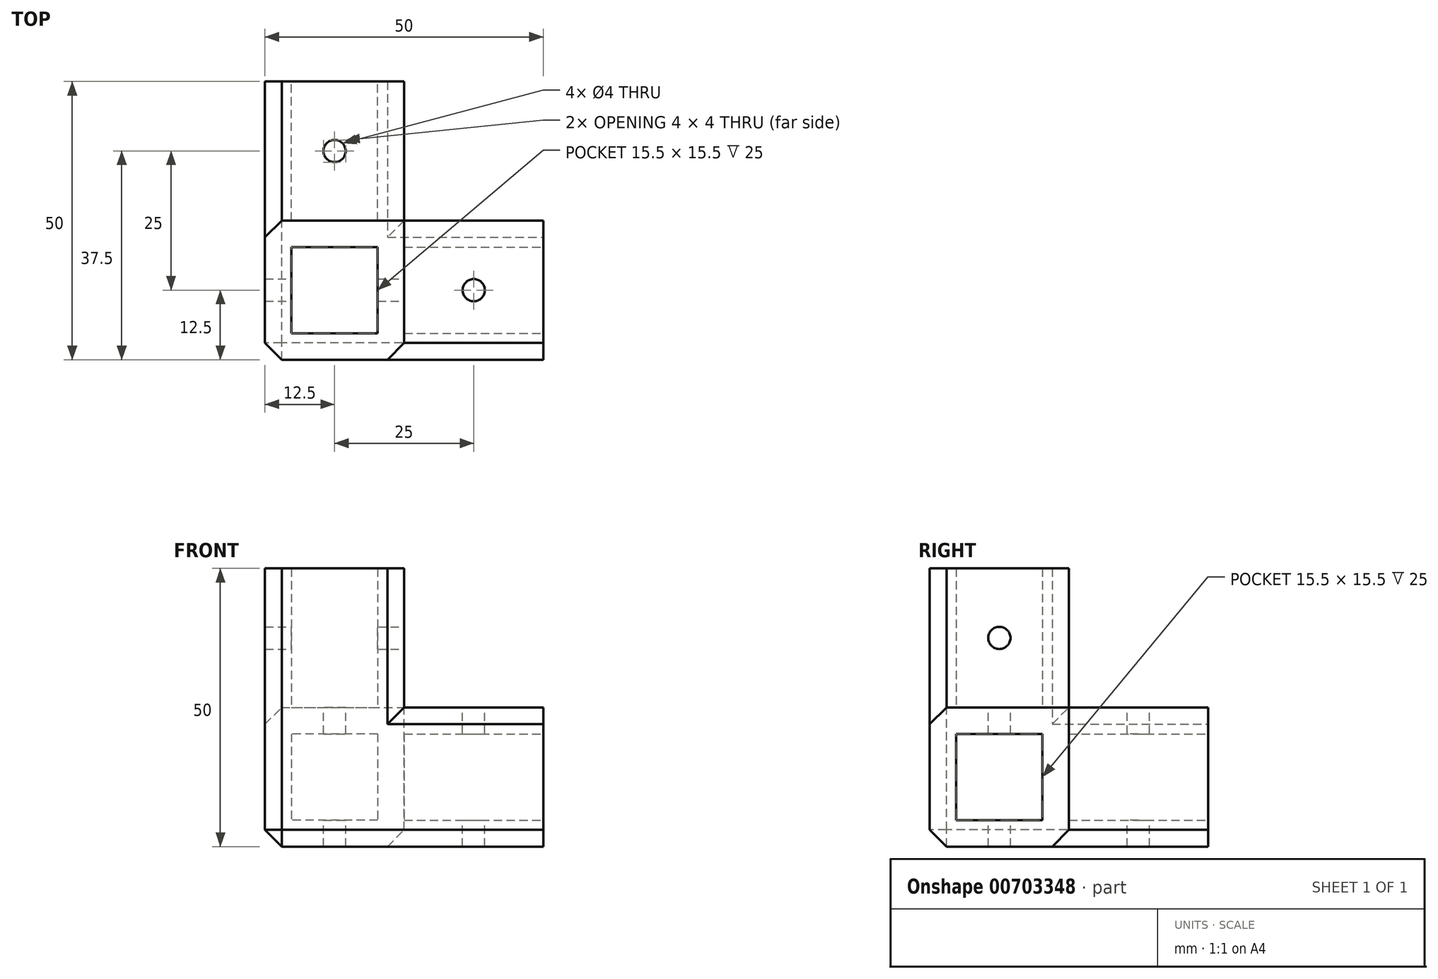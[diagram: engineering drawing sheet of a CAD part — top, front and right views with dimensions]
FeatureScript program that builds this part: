
annotation { "Feature Type Name" : "Feature", "Feature Type Description" : "" }
export const myFeature = defineFeature(function(context is Context, id is Id, definition is map)
    precondition{}
    {
        {
            var Q0;
            Q0=qCreatedBy(makeId("Top.planeOp"),FACE);
            var sketch = newSketch(context, id + "F0", { "sketchPlane" : qUnion([Q0])});
            skLineSegment(sketch, "E0", {"start": v(-60, 0) * mm, "end": v(-60, 50) * mm});
            skLineSegment(sketch, "E1", {"start": v(-60, 50) * mm, "end": v(-35, 50) * mm});
            skLineSegment(sketch, "E2", {"start": v(-35, 50) * mm, "end": v(-35, 25) * mm});
            skLineSegment(sketch, "E3", {"start": v(-35, 25) * mm, "end": v(-10, 25) * mm});
            skLineSegment(sketch, "E4", {"start": v(-10, 25) * mm, "end": v(-10, 0) * mm});
            skLineSegment(sketch, "E5", {"start": v(-10, 0) * mm, "end": v(-60, 0) * mm});
            skLineSegment(sketch, "E6", {"start": v(-60, 25) * mm, "end": v(-35, 25) * mm});
            skLineSegment(sketch, "E7", {"start": v(-35, 25) * mm, "end": v(-35, 0) * mm});
            skLineSegment(sketch, "E8", {"start": v(-60, 0) * mm, "end": v(-35, 25) * mm, "construction": true});
            skLineSegment(sketch, "E9", {"start": v(-60, 25) * mm, "end": v(-35, 0) * mm, "construction": true});
            skLineSegment(sketch, "E10.bottom", {"start": v(-55.25, 20.25) * mm, "end": v(-39.75, 20.25) * mm});
            skLineSegment(sketch, "E10.top", {"start": v(-55.25, 4.75) * mm, "end": v(-39.75, 4.75) * mm});
            skLineSegment(sketch, "E10.left", {"start": v(-55.25, 20.25) * mm, "end": v(-55.25, 4.75) * mm});
            skLineSegment(sketch, "E10.right", {"start": v(-39.75, 20.25) * mm, "end": v(-39.75, 4.75) * mm});
            skPoint(sketch, "E10.middle", {"position": v(-47.5, 12.5) * mm});
            skLineSegment(sketch, "E11", {"start": v(-35, 0) * mm, "end": v(-10, 25) * mm, "construction": true});
            skLineSegment(sketch, "E12", {"start": v(-10, 0) * mm, "end": v(-60, 50) * mm, "construction": true});
            skLineSegment(sketch, "E13", {"start": v(-60, 25) * mm, "end": v(-35, 50) * mm, "construction": true});
            skCircle(sketch, "E14", {"center": v(-47.5, 37.5) * mm, "radius": 2 * mm});
            skCircle(sketch, "E15", {"center": v(-22.5, 12.5) * mm, "radius": 2 * mm});
            skSolve(sketch);
        }
        {
            var Q0;
            {var subQ0=sQuery(id+"F0.wireOp",EDGE,"E1");Q0=makeQuery(id+"F0.imprint","IMPRINT",FACE,{"disambiguationData":[TD([[makeQuery(id+"F0.imprint","IMPRINT",EDGE,{"derivedFrom":subQ0}),-1.0]])]});}
            var Q1;
            Q1=makeQuery(id+"F0.imprint","IMPRINT",FACE,{"disambiguationData":[TD([[makeQuery(id+"F0.imprint","IMPRINT",EDGE,{"derivedFrom":sQuery(id+"F0.wireOp",EDGE,"E3")}),-1.0]])]});
            var Q2;
            {var subQ1=sQuery(id+"F0.wireOp",EDGE,"E6");Q2=makeQuery(id+"F0.imprint","IMPRINT",FACE,{"disambiguationData":[TD([[makeQuery(id+"F0.imprint","IMPRINT",EDGE,{"derivedFrom":subQ1}),-1.0]])]});}
            var Q3;
            Q3=makeQuery(id+"F0.imprint","IMPRINT",FACE,{"disambiguationData":[TD([[makeQuery(id+"F0.imprint","IMPRINT",EDGE,{"derivedFrom":sQuery(id+"F0.wireOp",EDGE,"E10.bottom")}),-1.0]])]});
            extrude(context, id + "F1", {"entities" : qUnion([Q0, Q1, Q2, Q3]), "oppositeDirection" : true, "depth" : 25 * mm, "offsetDistance" : 25 * mm});
        }
        {
            var Q0;
            Q0=makeQuery(id+"F1.opExtrude","SWEPT_FACE",FACE,{"disambiguationData":[OSD([sQuery(id+"F0.wireOp",EDGE,"E4")])]});
            var sketch = newSketch(context, id + "F2", { "sketchPlane" : qUnion([Q0])});
            skLineSegment(sketch, "E16", {"start": v(0, 0) * mm, "end": v(25, -25) * mm, "construction": true});
            skLineSegment(sketch, "E17", {"start": v(25, -25) * mm, "end": v(25, 0) * mm, "construction": true});
            skLineSegment(sketch, "E18", {"start": v(25, 0) * mm, "end": v(0, -25) * mm, "construction": true});
            skLineSegment(sketch, "E19.bottom", {"start": v(4.75, -4.75) * mm, "end": v(20.25, -4.75) * mm});
            skLineSegment(sketch, "E19.top", {"start": v(4.75, -20.25) * mm, "end": v(20.25, -20.25) * mm});
            skLineSegment(sketch, "E19.left", {"start": v(4.75, -4.75) * mm, "end": v(4.75, -20.25) * mm});
            skLineSegment(sketch, "E19.right", {"start": v(20.25, -4.75) * mm, "end": v(20.25, -20.25) * mm});
            skPoint(sketch, "E19.middle", {"position": v(12.5, -12.5) * mm});
            skSolve(sketch);
        }
        {
            var Q0;
            Q0=makeQuery(id+"F2.imprint","IMPRINT",FACE,{"disambiguationData":[TD([[makeQuery(id+"F2.imprint","IMPRINT",EDGE,{"derivedFrom":sQuery(id+"F2.wireOp",EDGE,"E19.bottom")}),-1.0]])]});
            extrude(context, id + "F3", {"entities" : qUnion([Q0]), "operationType" : NewBodyOperationType.REMOVE, "oppositeDirection" : true, "depth" : 25 * mm, "offsetDistance" : 25 * mm});
        }
        {
            var Q0;
            Q0=makeQuery(id+"F1.opExtrude","SWEPT_FACE",FACE,{"disambiguationData":[OSD([sQuery(id+"F0.wireOp",EDGE,"E1")])]});
            var sketch = newSketch(context, id + "F4", { "sketchPlane" : qUnion([Q0])});
            skLineSegment(sketch, "E20", {"start": v(35, 0) * mm, "end": v(60, -25) * mm, "construction": true});
            skLineSegment(sketch, "E21", {"start": v(60, -25) * mm, "end": v(60, 0) * mm, "construction": true});
            skLineSegment(sketch, "E22", {"start": v(60, 0) * mm, "end": v(35, -25) * mm, "construction": true});
            skLineSegment(sketch, "E23.bottom", {"start": v(39.75, -4.75) * mm, "end": v(55.25, -4.75) * mm});
            skLineSegment(sketch, "E23.top", {"start": v(39.75, -20.25) * mm, "end": v(55.25, -20.25) * mm});
            skLineSegment(sketch, "E23.left", {"start": v(39.75, -4.75) * mm, "end": v(39.75, -20.25) * mm});
            skLineSegment(sketch, "E23.right", {"start": v(55.25, -4.75) * mm, "end": v(55.25, -20.25) * mm});
            skPoint(sketch, "E23.middle", {"position": v(47.5, -12.5) * mm});
            skSolve(sketch);
        }
        {
            var Q0;
            Q0=makeQuery(id+"F4.imprint","IMPRINT",FACE,{"disambiguationData":[TD([[makeQuery(id+"F4.imprint","IMPRINT",EDGE,{"derivedFrom":sQuery(id+"F4.wireOp",EDGE,"E23.bottom")}),-1.0]])]});
            extrude(context, id + "F5", {"entities" : qUnion([Q0]), "operationType" : NewBodyOperationType.REMOVE, "oppositeDirection" : true, "depth" : 25 * mm, "offsetDistance" : 25 * mm});
        }
        {
            var Q0;
            {var subQ1=sQuery(id+"F0.wireOp",EDGE,"E6");Q0=makeQuery(id+"F0.imprint","IMPRINT",FACE,{"disambiguationData":[TD([[makeQuery(id+"F0.imprint","IMPRINT",EDGE,{"derivedFrom":subQ1}),-1.0]])]});}
            extrude(context, id + "F6", {"entities" : qUnion([Q0]), "operationType" : NewBodyOperationType.ADD, "depth" : 25 * mm, "offsetDistance" : 25 * mm});
        }
        {
            var Q0;
            Q0=makeQuery(id+"F6.opExtrude","SWEPT_FACE",FACE,{"disambiguationData":[OSD([sQuery(id+"F0.wireOp",EDGE,"E7")])]});
            var sketch = newSketch(context, id + "F7", { "sketchPlane" : qUnion([Q0])});
            skLineSegment(sketch, "E24", {"start": v(25, 0) * mm, "end": v(0, 25) * mm, "construction": true});
            skLineSegment(sketch, "E25", {"start": v(0, 25) * mm, "end": v(25, 25) * mm, "construction": true});
            skLineSegment(sketch, "E26", {"start": v(25, 25) * mm, "end": v(0, 0) * mm, "construction": true});
            skCircle(sketch, "E27", {"center": v(12.5, 12.5) * mm, "radius": 2 * mm});
            skSolve(sketch);
        }
        {
            var Q0;
            {var subQ0=sQuery(id+"F0.wireOp",EDGE,"E5");var subQ1=sQuery(id+"F0.wireOp",EDGE,"E0");Q0=makeQuery(id+"F6.boolean.opBoolean","MERGE",EDGE,{"derivedFrom":[makeQuery(id+"F1.opExtrude","SWEPT_EDGE",EDGE,{"disambiguationData":[OSD([subQ1,subQ0])]}),makeQuery(id+"F6.opExtrude","SWEPT_EDGE",EDGE,{"disambiguationData":[OSD([subQ1,subQ0])]})]});}
            var Q1;
            Q1=makeQuery(id+"F1.opExtrude","CAP_EDGE",EDGE,{"disambiguationData":[OSD([sQuery(id+"F0.wireOp",EDGE,"E5")])],"isStart":false});
            var Q2;
            Q2=makeQuery(id+"F1.opExtrude","CAP_EDGE",EDGE,{"disambiguationData":[OSD([sQuery(id+"F0.wireOp",EDGE,"E0")])],"isStart":false});
            var Q3;
            Q3=makeQuery(id+"F6.opExtrude","SWEPT_EDGE",EDGE,{"disambiguationData":[OSD([sQuery(id+"F0.wireOp",EDGE,"E5"),sQuery(id+"F0.wireOp",EDGE,"E7")])]});
            var Q4;
            Q4=makeQuery(id+"F1.opExtrude","CAP_EDGE",EDGE,{"disambiguationData":[OSD([sQuery(id+"F0.wireOp",EDGE,"E5")])],"isStart":true});
            var Q5;
            Q5=makeQuery(id+"F1.opExtrude","CAP_EDGE",EDGE,{"disambiguationData":[OSD([sQuery(id+"F0.wireOp",EDGE,"E2")])],"isStart":false});
            var Q6;
            Q6=makeQuery(id+"F1.opExtrude","CAP_EDGE",EDGE,{"disambiguationData":[OSD([sQuery(id+"F0.wireOp",EDGE,"E3")])],"isStart":false});
            var Q7;
            Q7=makeQuery(id+"F1.opExtrude","CAP_EDGE",EDGE,{"disambiguationData":[OSD([sQuery(id+"F0.wireOp",EDGE,"E0")])],"isStart":true});
            var Q8;
            Q8=makeQuery(id+"F6.opExtrude","SWEPT_EDGE",EDGE,{"disambiguationData":[OSD([sQuery(id+"F0.wireOp",EDGE,"E0"),sQuery(id+"F0.wireOp",EDGE,"E6")])]});
            chamfer(context, id + "F8", {"entities" : qUnion([Q0, Q1, Q2, Q3, Q4, Q5, Q6, Q7, Q8]), "width" : 3 * mm, "tangentPropagation" : true});
        }
        {
            var Q0;
            Q0=makeQuery(id+"F7.imprint","IMPRINT",FACE,{"disambiguationData":[TD([[makeQuery(id+"F7.imprint","IMPRINT",EDGE,{"derivedFrom":sQuery(id+"F7.wireOp",EDGE,"E27")}),1.0]])]});
            extrude(context, id + "F9", {"entities" : qUnion([Q0]), "operationType" : NewBodyOperationType.REMOVE, "oppositeDirection" : true, "depth" : 25 * mm, "offsetDistance" : 25 * mm});
        }
    });
